# Revit family: 1471xxx Fife 530
name_source: partatom
category: Lighting Fixtures
units: mm (PartAtom-declared; Revit-internal decimal feet)

## family parameters
Always vertical = Yes
Cut with Voids When Loaded = No
Host = Ceiling
Light Source = No
OmniClass Number = 23.80.70.11
OmniClass Title = Luminaries for Internal Lighting
Part Type = Normal
Room Calculation Point = No
Round Connector Dimension = Use Diameter
Shared = No

## types (2) — shared parameters
Dimmable = Yes
Dimming Method = Lamp Dependent
Driver Included = Not Applicable
Driver Required = No
Efficacy (lm/w) = Lamp Dependent
Electrical Class = 1
Lamp = LED
Length of supplied cable = Not Applicable
Light Source Fixed = Yes
Main Finish = Various
Main Material = Fabric
Manufacturer URL - Europe and Rest of World = www.astrolighting.com
Manufacturer URL - North America = us.astrolighting.com
Max Drop (pendants) = Not Applicable
Power (Watts) = Not Applicable
Product CCT = Lamp Dependent
Product CRI = Lamp Dependent
zero-valued in all types: Default Elevation

## per-type parameters (varying)
| type | ADA compliant | Location / IP Rating | Product Dimensions (MM) | Product Location | Product Name | Product SKU | Product Weight (KG) |
| CE | Not Applicable | IP20 | 145 x 530mm | Indoor | Fife 530 | 1471xxx | 2 mm  [stored 0.00656168 ft] |
| ETL |  |  | 145 x 330mm |  | Fife 330 | 1234567 | 0 mm  [stored 0 ft] |

note: [stored X ft] marks values corroborated as IEEE doubles in the binary element streams (Revit-internal decimal feet)

## geometry (parser evidence)
native form markers: Sweep x3
no freeform markers — native parametric forms only
